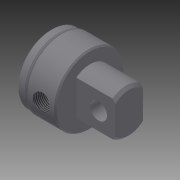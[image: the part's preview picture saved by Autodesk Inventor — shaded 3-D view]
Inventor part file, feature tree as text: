
AUTODESK INVENTOR PART (.ipt)
format: ipt  version: 2014 (Build 180170000, 170)  size: 260,608 bytes
history: native  units: in
note: dims shown in document units (in); Inventor stores cm internally (conversion verified against a paired STEP export)
features: other x126, sketch x8, revolve x5, extrude x2, hole x1, thread x1
ambient origin geometry x8: Origin, YZ Plane, XZ Plane, XY Plane, X Axis, Y Axis, Z Axis, Center Point
bodies: Solid1 (feature_tree)
feature tree (143):
  revolve  "Revolution1"  Angle=360.0deg
  revolve  "Revolution2"  Angle=360.0deg
  extrude  "Extrusion1"  TaperAngle=360.0deg  [1 undecoded]
  hole  "Hole1"  [1 undecoded]
  revolve  "Revolution3"  [1 undecoded]
  thread  "Thread1"  [1 undecoded]
  revolve  "Revolution4"  [1 undecoded]
  revolve  "Revolution5"  [1 undecoded]
  extrude  "Extrusion2"  [1 undecoded]
  other  "f_XY"
  other  "f_YZ"
  other  "f_ZX"
  other  "f_X"
  other  "f_Y"
  other  "f_Z"
  other  "f_Center"
  other  "lovra1_XY"
  other  "lovra1_YZ"
  other  "lovra1_ZX"
  other  "lovra1_X"
  other  "lovra1_Y"
  other  "lovra1_Z"
  other  "lovra1_Center"
  other  "lovra2_XY"
  other  "lovra2_YZ"
  other  "lovra2_ZX"
  other  "lovra2_X"
  other  "lovra2_Y"
  other  "lovra2_Z"
  other  "lovra2_Center"
  other  "lovra21_XY"
  other  "lovra21_YZ"
  other  "lovra21_ZX"
  other  "lovra21_X"
  other  "lovra21_Y"
  other  "lovra21_Z"
  other  "lovra21_Center"
  other  "lovra22_XY"
  other  "lovra22_YZ"
  other  "lovra22_ZX"
  other  "lovra22_X"
  other  "lovra22_Y"
  other  "lovra22_Z"
  other  "lovra22_Center"
  other  "lovra3_XY"
  other  "lovra3_YZ"
  other  "lovra3_ZX"
  other  "lovra3_X"
  other  "lovra3_Y"
  other  "lovra3_Z"
  other  "lovra3_Center"
  other  "olen_XY"
  other  "olen_YZ"
  other  "olen_ZX"
  other  "olen_X"
  other  "olen_Y"
  other  "olen_Z"
  other  "olen_Center"
  other  "p1_XY"
  other  "p1_YZ"
  other  "p1_ZX"
  other  "p1_X"
  other  "p1_Y"
  other  "p1_Z"
  other  "p1_Center"
  other  "p2_XY"
  other  "p2_YZ"
  other  "p2_ZX"
  other  "p2_X"
  other  "p2_Y"
  other  "p2_Z"
  other  "p2_Center"
  other  "port_XY"
  other  "port_YZ"
  other  "port_ZX"
  other  "port_X"
  other  "port_Y"
  other  "port_Z"
  other  "port_Center"
  other  "port2_XY"
  other  "port2_YZ"
  other  "port2_ZX"
  other  "port2_X"
  other  "port2_Y"
  other  "port2_Z"
  other  "port2_Center"
  other  "thd1_XY"
  other  "thd1_YZ"
  other  "thd1_ZX"
  other  "thd1_X"
  other  "thd1_Y"
  other  "thd1_Z"
  other  "thd1_Center"
  other  "thd2_XY"
  other  "thd2_YZ"
  other  "thd2_ZX"
  other  "thd2_X"
  other  "thd2_Y"
  other  "thd2_Z"
  other  "thd2_Center"
  other  "to_mounting_bracket_XY"
  other  "to_mounting_bracket_YZ"
  other  "to_mounting_bracket_ZX"
  other  "to_mounting_bracket_X"
  other  "to_mounting_bracket_Y"
  other  "to_mounting_bracket_Z"
  other  "to_mounting_bracket_Center"
  other  "to_nut_XY"
  other  "to_nut_YZ"
  other  "to_nut_ZX"
  other  "to_nut_X"
  other  "to_nut_Y"
  other  "to_nut_Z"
  other  "to_nut_Center"
  other  "to_pin_XY"
  other  "to_pin_YZ"
  other  "to_pin_ZX"
  other  "to_pin_X"
  other  "to_pin_Y"
  other  "to_pin_Z"
  other  "to_pin_Center"
  other  "to_screw_XY"
  other  "to_screw_YZ"
  other  "to_screw_ZX"
  other  "to_screw_X"
  other  "to_screw_Y"
  other  "to_screw_Z"
  other  "to_screw_Center"
  other  "to_tube_XY"
  other  "to_tube_YZ"
  other  "to_tube_ZX"
  other  "to_tube_X"
  other  "to_tube_Y"
  other  "to_tube_Z"
  other  "to_tube_Center"
  sketch  "Sketch_18"  dims[d4=0.532in d5=0.75in d6=0.375in d7=0.25in d8=0.5635in d9=0.8052in d10=120.0deg d11=360.0deg]
  sketch  "Sketch_21"  dims[d15=360.0deg d16=0.9255in d17=0.0in]
  sketch  "Sketch_9"  dims[d2=0.875in d3=0.0in]
  sketch  "Sketch4"  dims[d0=360.0deg d1=360.0deg]
  sketch  "Sketch_68"
  sketch  "Sketch_20"  dims[d12=0.2731in d13=0.0in d14=360.0deg]
  sketch  "Sketch_24"
  sketch  "Sketch_43"
note: 7 required parameter values undecoded (feature->parameter linkage not recoverable at this tier; creation-order binding heuristic only, values carry confidence <= 0.55)
